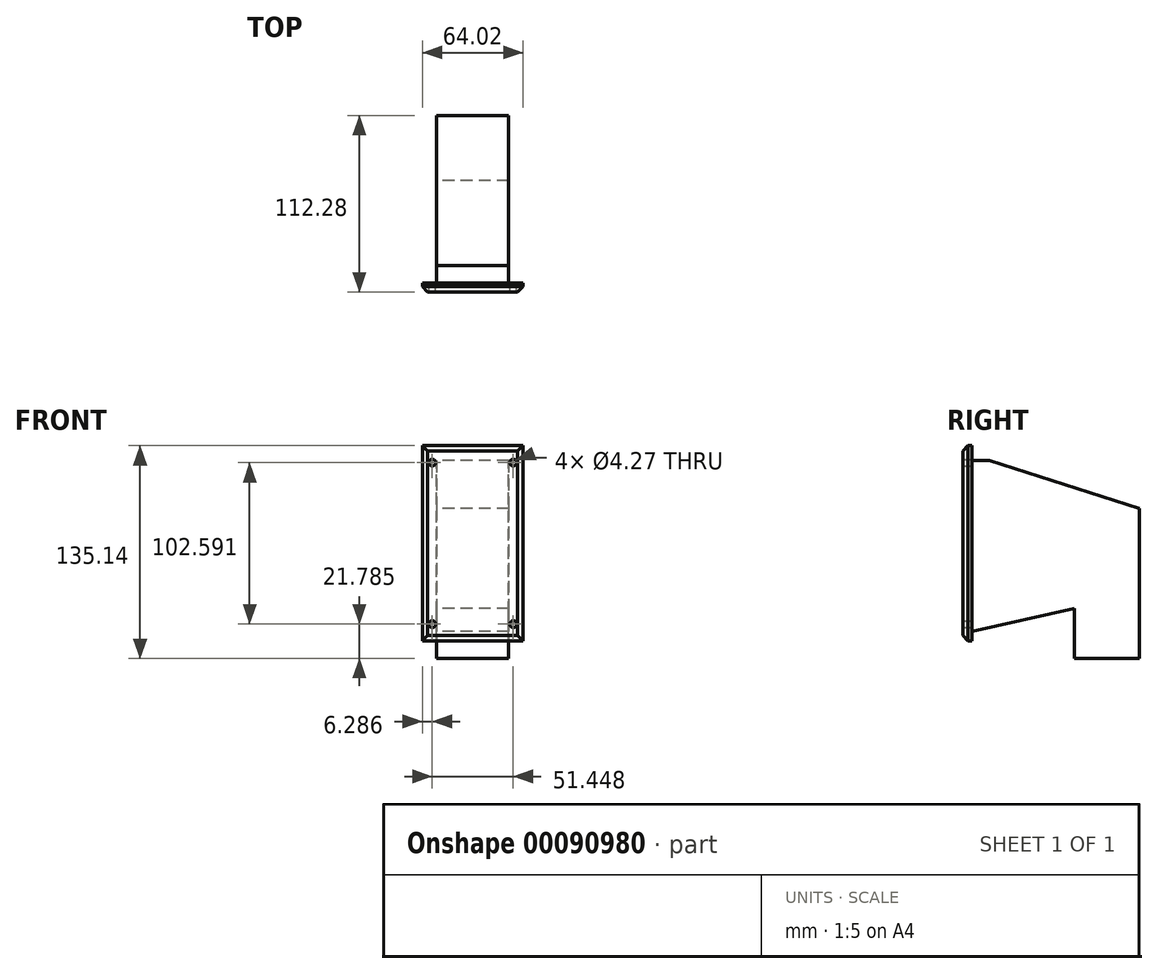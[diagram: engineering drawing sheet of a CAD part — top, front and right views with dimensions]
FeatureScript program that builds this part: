
annotation { "Feature Type Name" : "Feature", "Feature Type Description" : "" }
export const myFeature = defineFeature(function(context is Context, id is Id, definition is map)
    precondition{}
    {
        {
            var Q0;
            Q0=qCreatedBy(makeId("Front.planeOp"),FACE);
            var sketch = newSketch(context, id + "F0", { "sketchPlane" : qUnion([Q0])});
            skLineSegment(sketch, "E0.bottom", {"start": v(32.01, 62.06) * mm, "end": v(-32.01, 62.06) * mm});
            skLineSegment(sketch, "E0.top", {"start": v(32.01, -62.06) * mm, "end": v(-32.01, -62.06) * mm});
            skLineSegment(sketch, "E0.left", {"start": v(32.01, 62.06) * mm, "end": v(32.01, -62.06) * mm});
            skLineSegment(sketch, "E0.right", {"start": v(-32.01, 62.06) * mm, "end": v(-32.01, -62.06) * mm});
            skPoint(sketch, "E0.middle", {"position": v(0, 0) * mm});
            skSolve(sketch);
        }
        {
            var Q0;
            Q0 = qSketchRegion(id + "F0", true);
            extrude(context, id + "F1", {"entities" : qUnion([Q0]), "depth" : 5.92 * mm});
        }
        {
            var Q0;
            Q0=makeQuery(id+"F1.opExtrude","CAP_FACE",FACE,{"disambiguationData":[OSD([sQuery(id+"F0.wireOp",EDGE,"E0.bottom"),sQuery(id+"F0.wireOp",EDGE,"E0.top"),sQuery(id+"F0.wireOp",EDGE,"E0.left"),sQuery(id+"F0.wireOp",EDGE,"E0.right")])],"isStart":true});
            var sketch = newSketch(context, id + "F2", { "sketchPlane" : qUnion([Q0])});
            skCircle(sketch, "E1", {"center": v(-25.72, 51.3) * mm, "radius": 2.13 * mm});
            skCircle(sketch, "E2", {"center": v(25.72, 51.3) * mm, "radius": 2.13 * mm});
            skCircle(sketch, "E3", {"center": v(25.72, -51.3) * mm, "radius": 2.13 * mm});
            skCircle(sketch, "E4", {"center": v(-25.72, -51.3) * mm, "radius": 2.13 * mm});
            skLineSegment(sketch, "E5", {"start": v(25.72, 51.3) * mm, "end": v(32.01, 51.3) * mm, "construction": true});
            skLineSegment(sketch, "E6", {"start": v(25.72, 62.06) * mm, "end": v(25.72, 51.3) * mm, "construction": true});
            skLineSegment(sketch, "E7", {"start": v(-25.72, 62.06) * mm, "end": v(-25.72, 51.3) * mm, "construction": true});
            skLineSegment(sketch, "E8", {"start": v(-25.72, 51.3) * mm, "end": v(-32.01, 51.3) * mm, "construction": true});
            skLineSegment(sketch, "E9", {"start": v(32.01, -51.3) * mm, "end": v(25.72, -51.3) * mm, "construction": true});
            skLineSegment(sketch, "E10", {"start": v(25.72, -62.06) * mm, "end": v(25.72, -51.3) * mm, "construction": true});
            skLineSegment(sketch, "E11", {"start": v(-25.72, -62.06) * mm, "end": v(-25.72, -51.3) * mm, "construction": true});
            skLineSegment(sketch, "E12", {"start": v(-32.01, -51.3) * mm, "end": v(-25.72, -51.3) * mm, "construction": true});
            skSolve(sketch);
        }
        {
            var Q0;
            Q0 = qSketchRegion(id + "F2", true);
            extrude(context, id + "F3", {"entities" : qUnion([Q0]), "operationType" : NewBodyOperationType.REMOVE, "endBound" : BoundingType.THROUGH_ALL, "oppositeDirection" : true, "depth" : 25.4 * mm});
        }
        {
            var Q0;
            Q0=makeQuery(id+"F1.opExtrude","CAP_EDGE",EDGE,{"disambiguationData":[OSD([sQuery(id+"F0.wireOp",EDGE,"E0.bottom")])],"isStart":false});
            var Q1;
            Q1=makeQuery(id+"F1.opExtrude","CAP_EDGE",EDGE,{"disambiguationData":[OSD([sQuery(id+"F0.wireOp",EDGE,"E0.right")])],"isStart":false});
            var Q2;
            Q2=makeQuery(id+"F1.opExtrude","CAP_EDGE",EDGE,{"disambiguationData":[OSD([sQuery(id+"F0.wireOp",EDGE,"E0.top")])],"isStart":false});
            var Q3;
            Q3=makeQuery(id+"F1.opExtrude","CAP_EDGE",EDGE,{"disambiguationData":[OSD([sQuery(id+"F0.wireOp",EDGE,"E0.left")])],"isStart":false});
            chamfer(context, id + "F4", {"entities" : qUnion([Q0, Q1, Q2, Q3]), "width" : 3.43 * mm, "tangentPropagation" : true});
        }
        {
            var Q0;
            Q0=qCreatedBy(makeId("Right.planeOp"),FACE);
            var sketch = newSketch(context, id + "F5", { "sketchPlane" : qUnion([Q0])});
            skLineSegment(sketch, "E13", {"start": v(0, 52.67) * mm, "end": v(11.11, 52.67) * mm});
            skLineSegment(sketch, "E14", {"start": v(11.11, 52.67) * mm, "end": v(106.36, 22.17) * mm});
            skLineSegment(sketch, "E15", {"start": v(106.36, 22.17) * mm, "end": v(106.36, -73.08) * mm});
            skLineSegment(sketch, "E16", {"start": v(106.36, -73.08) * mm, "end": v(65.09, -73.08) * mm});
            skLineSegment(sketch, "E17", {"start": v(65.09, -73.08) * mm, "end": v(65.09, -41.33) * mm});
            skLineSegment(sketch, "E18", {"start": v(65.09, -41.33) * mm, "end": v(0, -55.8) * mm});
            skLineSegment(sketch, "E19", {"start": v(0, -55.8) * mm, "end": v(0, 52.67) * mm});
            skSolve(sketch);
        }
        {
            var Q0;
            Q0 = qSketchRegion(id + "F5", true);
            extrude(context, id + "F6", {"entities" : qUnion([Q0]), "operationType" : NewBodyOperationType.ADD, "endBound" : BoundingType.SYMMETRIC, "depth" : 45.72 * mm});
        }
    });
